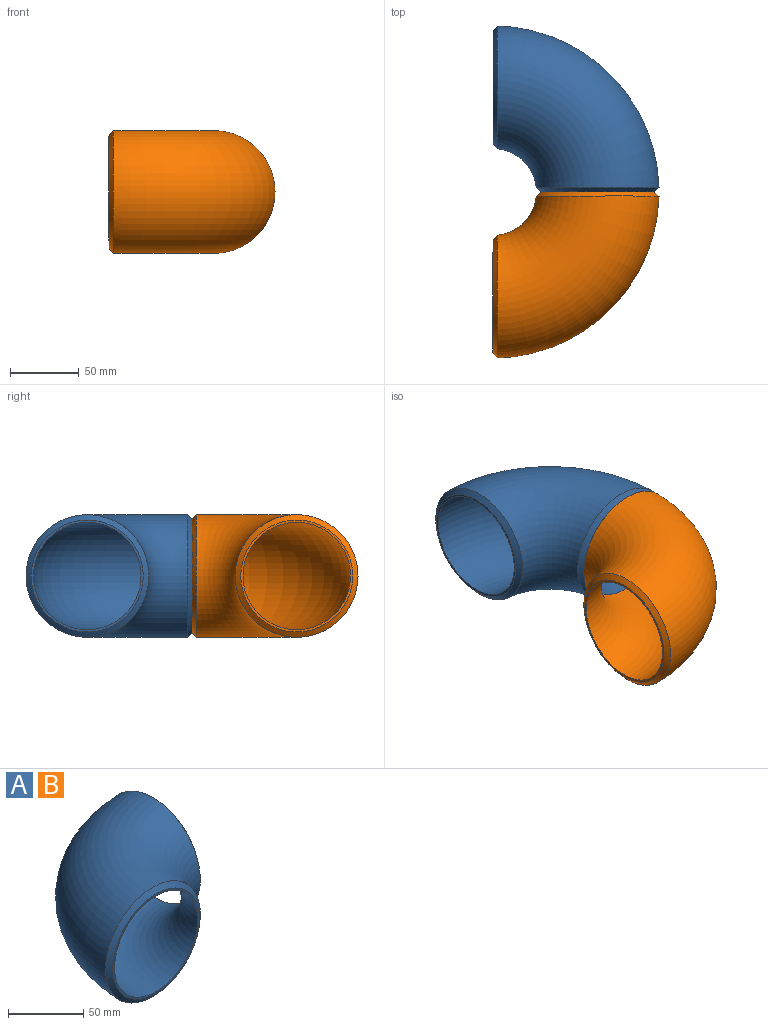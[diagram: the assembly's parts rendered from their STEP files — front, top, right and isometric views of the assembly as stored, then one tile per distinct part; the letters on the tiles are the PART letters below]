
ASSEMBLY  parts=2 mates=1
PART A: 6 faces, bbox 130.4x130.4x89.3 mm
  f0: torus R=76mm, axis (0,0,1), area 31134.9mm2, adj f2,f3
  f1: torus R=76mm, axis (0,0,1), area 29261mm2, adj f4,f5
  f2: cone r=45.8mm half-angle=52.5deg, axis (-1,0,0), area 1331.7mm2, adj f0,f4
  f3: cone r=45.8mm half-angle=52.5deg, axis (0,1,0), area 1331.7mm2, adj f0,f5
  f4: plane 81.22x81.22mm, normal (1,0,0), area 400.2mm2, adj f1,f2
  f5: plane 81.22x81.22mm, normal (0,-1,0), area 400.2mm2, adj f1,f3
PART B: same geometry as A
PLACE A rot(axis=(0,0,-1),90deg) t=(-60.11,2.43,84.22)mm
PLACE B rot(axis=(0.71,0.71,0),180deg) t=(-60.11,-149.57,84.22)mm
MATE fastened B.f2 <-> A.f2  axis (0,1,0) through (15.89,-73.57,84.22)mm
